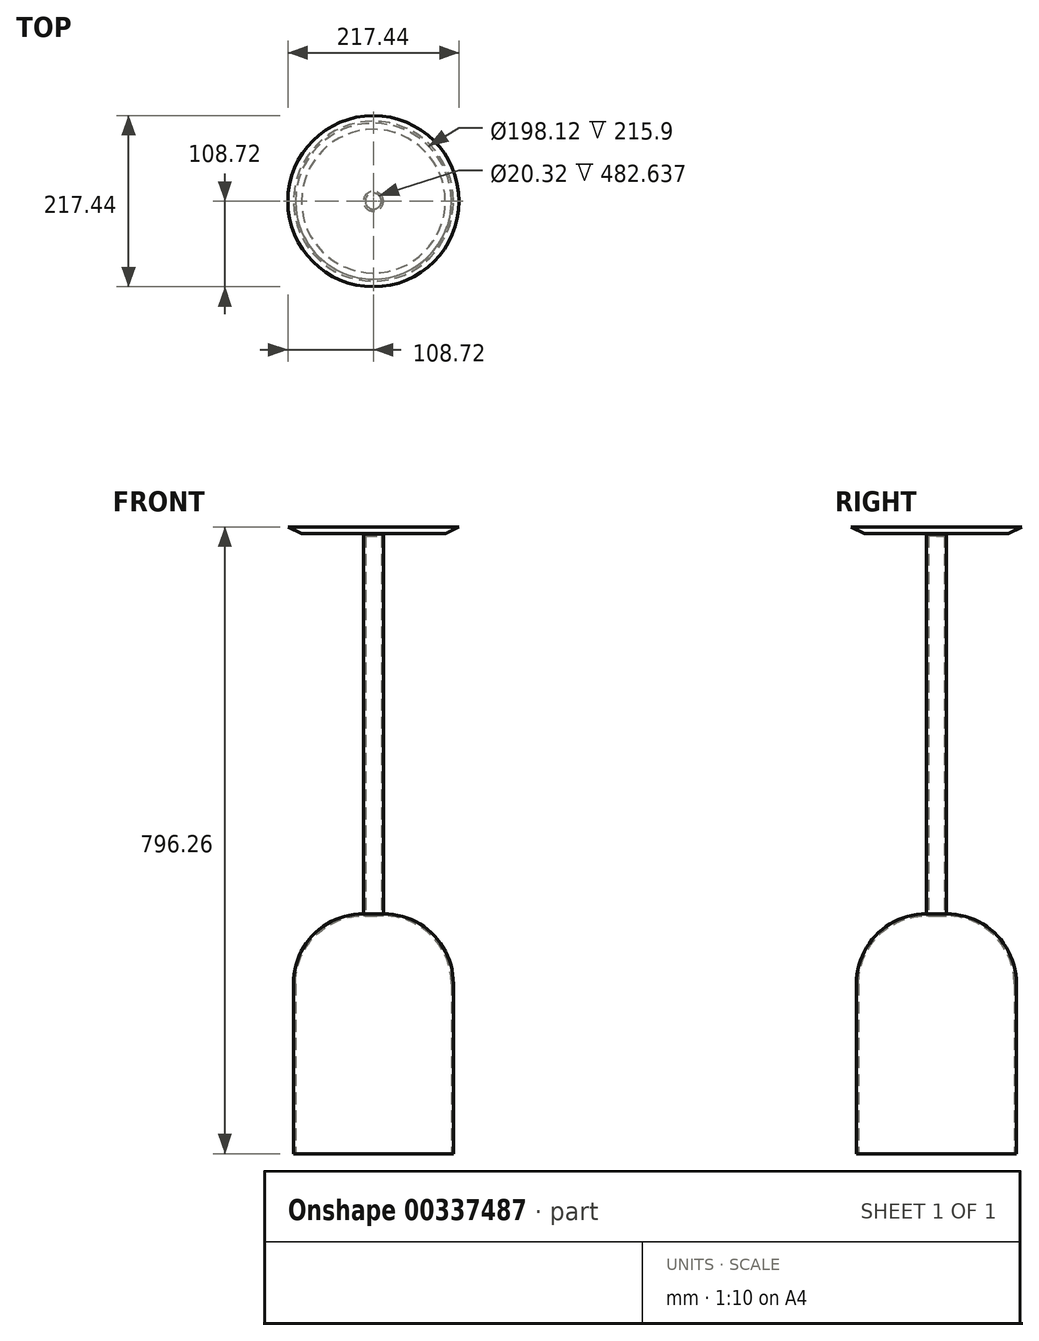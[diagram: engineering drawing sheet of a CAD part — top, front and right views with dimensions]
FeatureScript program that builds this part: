
annotation { "Feature Type Name" : "Feature", "Feature Type Description" : "" }
export const myFeature = defineFeature(function(context is Context, id is Id, definition is map)
    precondition{}
    {
        {
            var Q0;
            Q0=qCreatedBy(makeId("Top.planeOp"),FACE);
            var sketch = newSketch(context, id + "F0", { "sketchPlane" : qUnion([Q0])});
            skCircle(sketch, "E0", {"center": v(0, 0) * mm, "radius": 101.6 * mm});
            skSolve(sketch);
        }
        {
            var Q0;
            Q0=makeQuery(id+"F0.imprint","IMPRINT",FACE,{"disambiguationData":[TD([[makeQuery(id+"F0.imprint","IMPRINT",EDGE,{"derivedFrom":sQuery(id+"F0.wireOp",EDGE,"E0")}),1.0]])]});
            extrude(context, id + "F1", {"entities" : qUnion([Q0]), "depth" : 304.8 * mm});
        }
        {
            var Q0;
            Q0=makeQuery(id+"F1.opExtrude","CAP_FACE",FACE,{"disambiguationData":[OSD([sQuery(id+"F0.wireOp",EDGE,"E0")])],"isStart":false});
            fillet(context, id + "F2", {"entities" : qUnion([Q0]), "radius" : 88.9 * mm, "tangentPropagation" : true, "allowEdgeOverflow" : false});
        }
        {
            var Q0;
            Q0=makeQuery(id+"F1.opExtrude","CAP_FACE",FACE,{"disambiguationData":[OSD([sQuery(id+"F0.wireOp",EDGE,"E0")])],"isStart":false});
            extrude(context, id + "F3", {"entities" : qUnion([Q0]), "operationType" : NewBodyOperationType.ADD, "depth" : 482.6 * mm});
        }
        {
            var Q0;
            Q0=qCreatedBy(makeId("Front.planeOp"),FACE);
            var sketch = newSketch(context, id + "F4", { "sketchPlane" : qUnion([Q0])});
            skLineSegment(sketch, "E1", {"start": v(0, 787.58) * mm, "end": v(-91.24, 787.58) * mm});
            skLineSegment(sketch, "E2", {"start": v(-91.24, 787.58) * mm, "end": v(-108.72, 796.26) * mm});
            skLineSegment(sketch, "E3", {"start": v(-108.72, 796.26) * mm, "end": v(0, 796.26) * mm});
            skLineSegment(sketch, "E4", {"start": v(0, 796.26) * mm, "end": v(0, 775.69) * mm});
            skSolve(sketch);
        }
        {
            var Q0;
            {var subQ0=sQuery(id+"F4.wireOp",EDGE,"E1");Q0=makeQuery(id+"F4.imprint","IMPRINT",FACE,{"disambiguationData":[TD([[makeQuery(id+"F4.imprint","IMPRINT",EDGE,{"derivedFrom":subQ0}),-1.0]])]});}
            var Q1;
            Q1=sQuery(id+"F4.wireOp",EDGE,"E4");
            revolve(context, id + "F5", {"entities" : qUnion([Q0]), "axis" : qUnion([Q1]), "revolveType" : RevolveType.FULL});
        }
        {
            var Q0;
            Q0=makeQuery(id+"F1.opExtrude","CAP_FACE",FACE,{"disambiguationData":[OSD([sQuery(id+"F0.wireOp",EDGE,"E0")])],"isStart":true});
            shell(context, id + "F6", {"entities" : qUnion([Q0]), "thickness" : 2.54 * mm});
        }
    });
